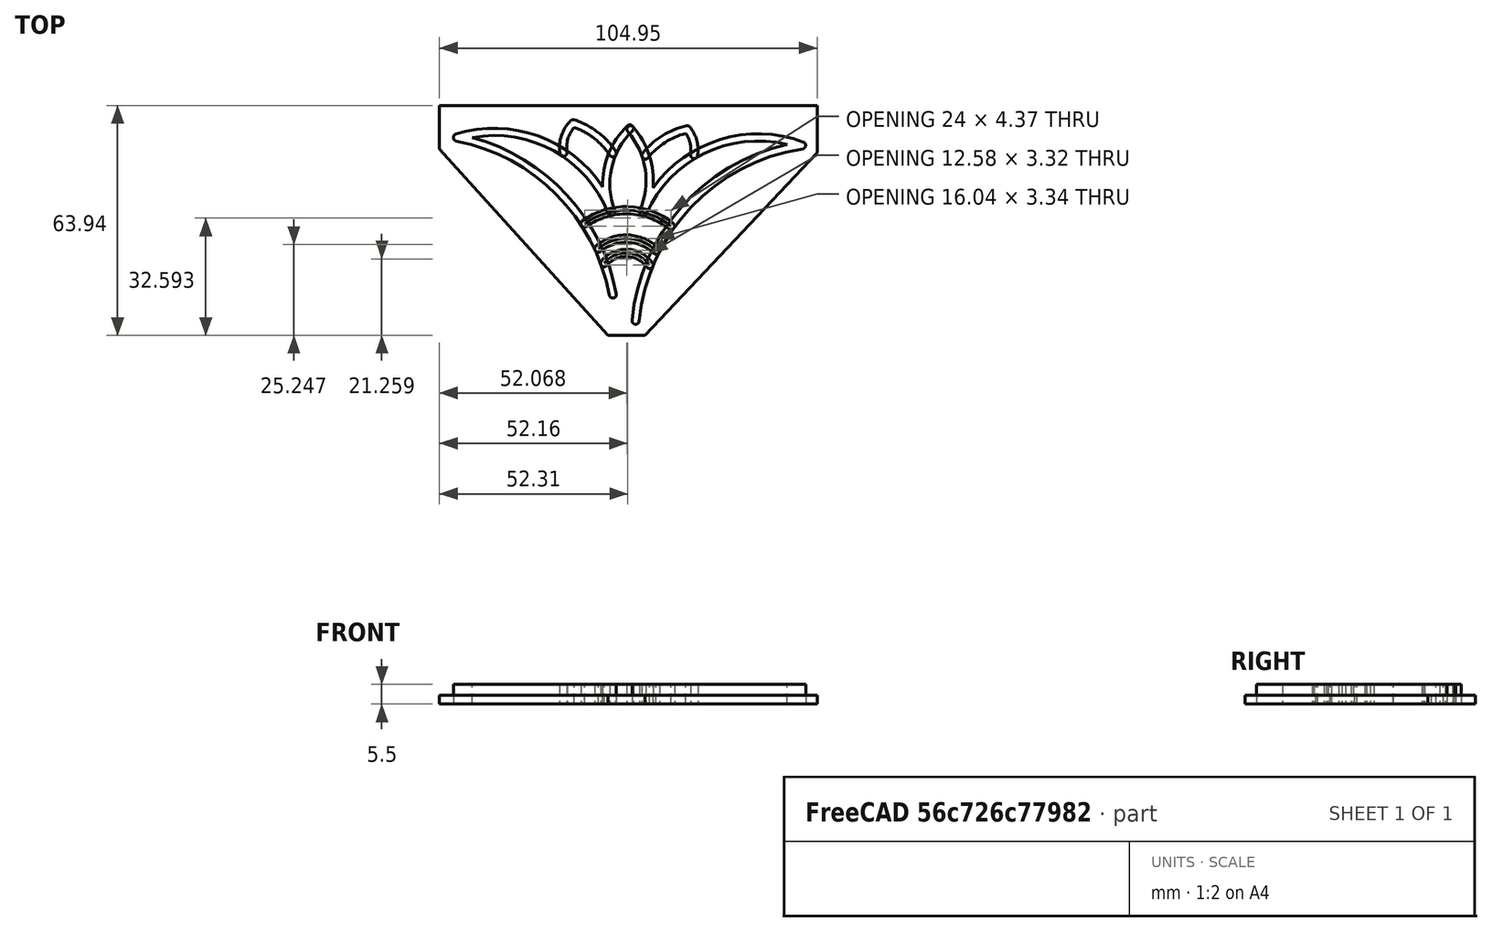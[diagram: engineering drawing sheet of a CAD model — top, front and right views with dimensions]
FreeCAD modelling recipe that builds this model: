
FCSTD DOCUMENT  (FreeCAD 0.20R27319 (Git))
Label: Bookend_Claire2
License: All rights reserved
LicenseURL: http://en.wikipedia.org/wiki/All_rights_reserved
objects: Sketcher::SketchObject×2, Part::Extrusion×2, Part::Mirroring×2, Image::ImagePlane×1, TechDraw::DrawSVGTemplate×1, TechDraw::DrawPage×1, Part::Offset2D×1, PartDesign::Body×1
note: 8 computed .brp shape members not serialized (recipe doc carries the construction recipe); baked Part::Feature solids carry a one-line shape summary decoded from their .brp

FEATURE [Sketcher::SketchObject] Sketch001
  FullyConstrained = false
  MapMode = 5
  Support = -> [XY_Plane001]
  sketch-geometry (41):
    g0: LineSegment StartX=0 StartY=0 StartZ=0 EndX=150 EndY=0 EndZ=0
    g1: LineSegment StartX=0 StartY=0 StartZ=0 EndX=0 EndY=150 EndZ=0
    g2: LineSegment StartX=0 StartY=150 StartZ=0 EndX=150 EndY=0 EndZ=0
    g3: LineSegment StartX=0 StartY=0 StartZ=0 EndX=91.2495 EndY=91.2495 EndZ=0
    g4: GeomPoint X=75.0281 Y=75.0281 Z=0
    g5: GeomPoint X=29.9813 Y=120.019 Z=0
    g6: GeomPoint X=59.9627 Y=90.0373 Z=0
    g7: GeomPoint X=89.944 Y=60.056 Z=0
    g8: GeomPoint X=119.925 Y=30.0747 Z=0
    g9: ArcOfCircle CenterX=33.7024 CenterY=33.7958 CenterZ=0 NormalX=0 NormalY=0 NormalZ=1 AngleXU=0 Radius=62.0702 StartAngle=0.436834 EndAngle=1.13396
    g10: ArcOfCircle CenterX=146.221 CenterY=86.3515 CenterZ=0 NormalX=0 NormalY=0 NormalZ=1 AngleXU=0 Radius=62.1171 StartAngle=3.5787 EndAngle=4.27528
    g11: ArcOfCircle CenterX=93.6298 CenterY=-26.2021 CenterZ=0 NormalX=0 NormalY=0 NormalZ=1 AngleXU=0 Radius=62.1171 StartAngle=0.437108 EndAngle=1.13369
    g12: ArcOfCircle CenterX=86.2581 CenterY=146.314 CenterZ=0 NormalX=0 NormalY=0 NormalZ=1 AngleXU=0 Radius=62.1171 StartAngle=3.5787 EndAngle=4.27528
    g13: ArcOfCircle CenterX=-26.2955 CenterY=93.7232 CenterZ=0 NormalX=0 NormalY=0 NormalZ=1 AngleXU=0 Radius=62.1171 StartAngle=0.437108 EndAngle=1.13369
    g14: LineSegment StartX=0 StartY=10 StartZ=0 EndX=155.016 EndY=10 EndZ=0
    g15: LineSegment StartX=10 StartY=149.907 StartZ=0 EndX=10 EndY=-0.000117613 EndZ=0
    g16: GeomPoint X=78.0897 Y=77.1833 Z=0
    g17: GeomPoint X=70.58 Y=70.58 Z=0
    g18: ArcOfCircle CenterX=27.0108 CenterY=27.894 CenterZ=0 NormalX=0 NormalY=0 NormalZ=1 AngleXU=0 Radius=60.9949 StartAngle=0.446588 EndAngle=1.12424
    g19: ArcOfCircle CenterX=138.266 CenterY=80.4834 CenterZ=0 NormalX=0 NormalY=0 NormalZ=1 AngleXU=0 Radius=62.065 StartAngle=3.57822 EndAngle=4.27543
    g20: ArcOfCircle CenterX=85.7052 CenterY=-32.021 CenterZ=0 NormalX=0 NormalY=0 NormalZ=1 AngleXU=0 Radius=62.1171 StartAngle=0.437108 EndAngle=1.13369
    g21: ArcOfCircle CenterX=79.654 CenterY=137.873 CenterZ=0 NormalX=0 NormalY=0 NormalZ=1 AngleXU=0 Radius=60.9371 StartAngle=3.58787 EndAngle=4.2661
    g22: ArcOfCircle CenterX=-30.2841 CenterY=85.2714 CenterZ=0 NormalX=0 NormalY=0 NormalZ=1 AngleXU=0 Radius=60.9371 StartAngle=0.446275 EndAngle=1.12451
    g23: LineSegment StartX=64.8329 StartY=64.6504 StartZ=0 EndX=67.8137 EndY=-0.435221 EndZ=0
    g24: LineSegment StartX=64.8329 StartY=64.6504 StartZ=0 EndX=0 EndY=64.6504 EndZ=0
    g25: ArcOfCircle CenterX=8.70334 CenterY=69.2919 CenterZ=0 NormalX=0 NormalY=0 NormalZ=1 AngleXU=0 Radius=54.672 StartAngle=4.90443 EndAngle=6.09853
    g26: ArcOfCircle CenterX=29.5089 CenterY=49.0527 CenterZ=0 NormalX=0 NormalY=0 NormalZ=1 AngleXU=0 Radius=34.9995 StartAngle=4.41156 EndAngle=5.90913
    g27: ArcOfCircle CenterX=81.9097 CenterY=28.4833 CenterZ=0 NormalX=0 NormalY=0 NormalZ=1 AngleXU=0 Radius=21.2938 StartAngle=2.76753 EndAngle=3.94942
    g28: ArcOfCircle CenterX=45.0723 CenterY=31.4173 CenterZ=0 NormalX=0 NormalY=0 NormalZ=1 AngleXU=0 Radius=20.7752 StartAngle=5.02352 EndAngle=5.6987
    g29: ArcOfCircle CenterX=58.0202 CenterY=18.3378 CenterZ=0 NormalX=0 NormalY=0 NormalZ=1 AngleXU=0 Radius=9.39503 StartAngle=2.98414 EndAngle=3.9353
    g30: ArcOfCircle CenterX=50.9616 CenterY=27.5926 CenterZ=0 NormalX=0 NormalY=0 NormalZ=1 AngleXU=0 Radius=21.7348 StartAngle=5.56662 EndAngle=6.70043
    g31: ArcOfCircle CenterX=87.6445 CenterY=33.4497 CenterZ=0 NormalX=0 NormalY=0 NormalZ=1 AngleXU=0 Radius=20.6183 StartAngle=3.81558 EndAngle=4.4911
    g32: ArcOfCircle CenterX=75.958 CenterY=19.072 CenterZ=0 NormalX=0 NormalY=0 NormalZ=1 AngleXU=0 Radius=9.17616 StartAngle=5.60767 EndAngle=6.43366
    g33: ArcOfCircle CenterX=102.829 CenterY=50.5838 CenterZ=0 NormalX=0 NormalY=0 NormalZ=1 AngleXU=0 Radius=34.9995 StartAngle=3.55884 EndAngle=5.06858
    g34: ArcOfCircle CenterX=123.193 CenterY=71.8408 CenterZ=0 NormalX=0 NormalY=0 NormalZ=1 AngleXU=0 Radius=54.672 StartAngle=3.23875 EndAngle=4.56258
    g35: ArcOfCircle CenterX=66.1581 CenterY=55.6698 CenterZ=0 NormalX=0 NormalY=0 NormalZ=1 AngleXU=0 Radius=19.828 StartAngle=4.08937 EndAngle=5.3901
    g36: ArcOfCircle CenterX=66.1581 CenterY=55.6698 CenterZ=0 NormalX=0 NormalY=0 NormalZ=1 AngleXU=0 Radius=7.96661 StartAngle=3.84065 EndAngle=5.66186
    g37: ArcOfCircle CenterX=66.1581 CenterY=55.6698 CenterZ=0 NormalX=0 NormalY=0 NormalZ=1 AngleXU=0 Radius=11.9655 StartAngle=4.00896 EndAngle=5.47943
    g38: ArcOfCircle CenterX=66.1581 CenterY=55.6698 CenterZ=0 NormalX=0 NormalY=0 NormalZ=1 AngleXU=0 Radius=7.96661 StartAngle=3.84065 EndAngle=5.66186
    g39: ArcOfCircle CenterX=66.1581 CenterY=55.6698 CenterZ=0 NormalX=0 NormalY=0 NormalZ=1 AngleXU=0 Radius=11.9655 StartAngle=4.00896 EndAngle=5.47943
    g40: ArcOfCircle CenterX=66.1581 CenterY=55.6698 CenterZ=0 NormalX=0 NormalY=0 NormalZ=1 AngleXU=0 Radius=19.828 StartAngle=4.08937 EndAngle=5.3901
  constraints (77):
    c: Coincident(g0,g-1)
    c: PointOnObject(g0,g-1)
    c: Distance(g0) = 150
    c: Coincident(g1,g0)
    c: PointOnObject(g1,g-2)
    c: Distance(g1) = 150
    c: Coincident(g2,g1)
    c: Coincident(g2,g0)
    c: Coincident(g3,g0)
    c: Angle(g0,g3) = 0.785398
    c: PointOnObject(g4,g3)
    c: PointOnObject(g5,g2)
    c: Distance(g5,g1) = 42.4
    c: PointOnObject(g6,g2)
    c: Distance(g5,g6) = 42.4
    c: PointOnObject(g7,g2)
    c: PointOnObject(g8,g2)
    c: Distance(g6,g7) = 42.4
    c: Distance(g7,g8) = 42.4
    c: Coincident(g9,g6)
    c: Coincident(g9,g7)
    c: PointOnObject(g14,g1)
    c: Horizontal(g14)
    c: Distance(g14,g0) = 10
    c: Vertical(g15)
    c: Distance(g0,g15) = 10
    c: PointOnObject(g16,g9)
    c: PointOnObject(g17,g3)
    c: Distance(g17,g16) = 10
    c: PointOnObject(g17,g18)
    c: Coincident(g19,g18)
    c: Coincident(g24,g23)
    c: PointOnObject(g24,g1)
    c: Horizontal(g24)
    c: Coincident(g26,g25)
    c: PointOnObject(g27,g23)
    c: PointOnObject(g28,g27)
    c: Coincident(g29,g28)
    c: PointOnObject(g29,g26)
    c: PointOnObject(g31,g30)
    c: Coincident(g32,g31)
    c: PointOnObject(g32,g33)
    c: Coincident(g34,g33)
    c: PointOnObject(g35,g34)
    c: PointOnObject(g35,g25)
    c: PointOnObject(g36,g25)
    c: PointOnObject(g36,g34)
    c: PointOnObject(g37,g25)
    c: PointOnObject(g37,g34)
    c: PointOnObject(g26,g35)
    c: PointOnObject(g30,g35)
    c: Coincident(g36,g37)
    c: Tangent(g27,g26) = 1.5708
    c: Tangent(g30,g33) = 1.5708
    c: Equal(g25,g34)
    c: Equal(g26,g33)
    c: Block(g25)
    c: Block(g34)
    c: Block(g36)
    c: Block(g37)
    c: Block(g35)
    c: Block(g33)
    c: Block(g30)
    c: Block(g27)
    c: Block(g26)
    c: Block(g29)
    c: Block(g32)
    c: Block(g28)
    c: Block(g31)
    c: Coincident(g38,g36)
    c: Coincident(g38,g36)
    c: Coincident(g39,g37)
    c: Coincident(g39,g37)
    c: Tangent(g39,g37)
    c: Coincident(g40,g35)
    c: Coincident(g40,g35)
    c: Tangent(g40,g35)
FEATURE [Image::ImagePlane] ImagePlane
  Placement = pos=(44,43,0) rot=(0,0,1;5.49779rad)
  XSize = 116
  YSize = 70
FEATURE [TechDraw::DrawSVGTemplate] Template
  EditableTexts = Designed_by_Name=Designed by Name; Drawing_number=Drawing number; FC-Date=Date; FC-SC=Scale; FC-SH=Sheet; FC-Title=Title; Subtitle=Subtitle; Weight=Weight
  Height = 210
  Orientation = 1
  Width = 297
FEATURE [TechDraw::DrawPage] Page
  KeepUpdated = true
  NextBalloonIndex = 1
  ProjectionType = 0
  Template = -> Template
FEATURE [Part::Offset2D] Offset2D
  Fill = true
  Intersection = false
  Join = 0
  Mode = 1
  SelfIntersection = false
  Source = -> Sketch001
  Value = 1
FEATURE [Part::Extrusion] Extrude
  Base = -> Offset2D
  Dir = (0,0,1)
  DirMode = 2
  FaceMakerClass = Part::FaceMakerBullseye
  LengthFwd = 5.5
  LengthRev = 0
  Solid = false
  Symmetric = false
FEATURE [Sketcher::SketchObject] Sketch
  FullyConstrained = false
  MapMode = 5
  Support = -> [XY_Plane001]
  sketch-geometry (6):
    g0: LineSegment StartX=14.2826 StartY=6.68597 StartZ=0 EndX=14.2826 EndY=18.8478 EndZ=0
    g1: LineSegment StartX=14.2826 StartY=18.8478 StartZ=0 EndX=61.1643 EndY=70.6335 EndZ=0
    g2: LineSegment StartX=61.1643 StartY=70.6335 StartZ=0 EndX=71.3646 EndY=70.6335 EndZ=0
    g3: LineSegment StartX=71.3646 StartY=70.6335 StartZ=0 EndX=119.227 EndY=19.8286 EndZ=0
    g4: LineSegment StartX=119.227 StartY=19.8286 StartZ=0 EndX=119.227 EndY=6.68597 EndZ=0
    g5: LineSegment StartX=119.227 StartY=6.68597 StartZ=0 EndX=14.2826 EndY=6.68597 EndZ=0
  constraints (10):
    c: Vertical(g0)
    c: Coincident(g0,g1)
    c: Coincident(g1,g2)
    c: Horizontal(g2)
    c: Coincident(g2,g3)
    c: Coincident(g3,g4)
    c: Vertical(g4)
    c: Coincident(g4,g5)
    c: Coincident(g5,g0)
    c: Horizontal(g5)
FEATURE [PartDesign::Body] Body001
  Group = -> [Sketch001,Sketch]
  Origin = -> Origin001
FEATURE [Part::Extrusion] Extrude002
  Base = -> Sketch
  Dir = (0,0,1)
  DirMode = 2
  FaceMakerClass = Part::FaceMakerBullseye
  LengthFwd = 2.5
  LengthRev = 0
  Solid = true
  Symmetric = false
FEATURE [Part::Mirroring] Part__Mirroring  label="Extrude (Mirror #1)"
  Base = (0,0,0)
  Normal = (0,1,0)
  Source = -> Extrude
FEATURE [Part::Mirroring] Part__Mirroring001  label="Extrude002 (Mirror #2)"
  Base = (0,0,0)
  Normal = (0,1,0)
  Source = -> Extrude002
